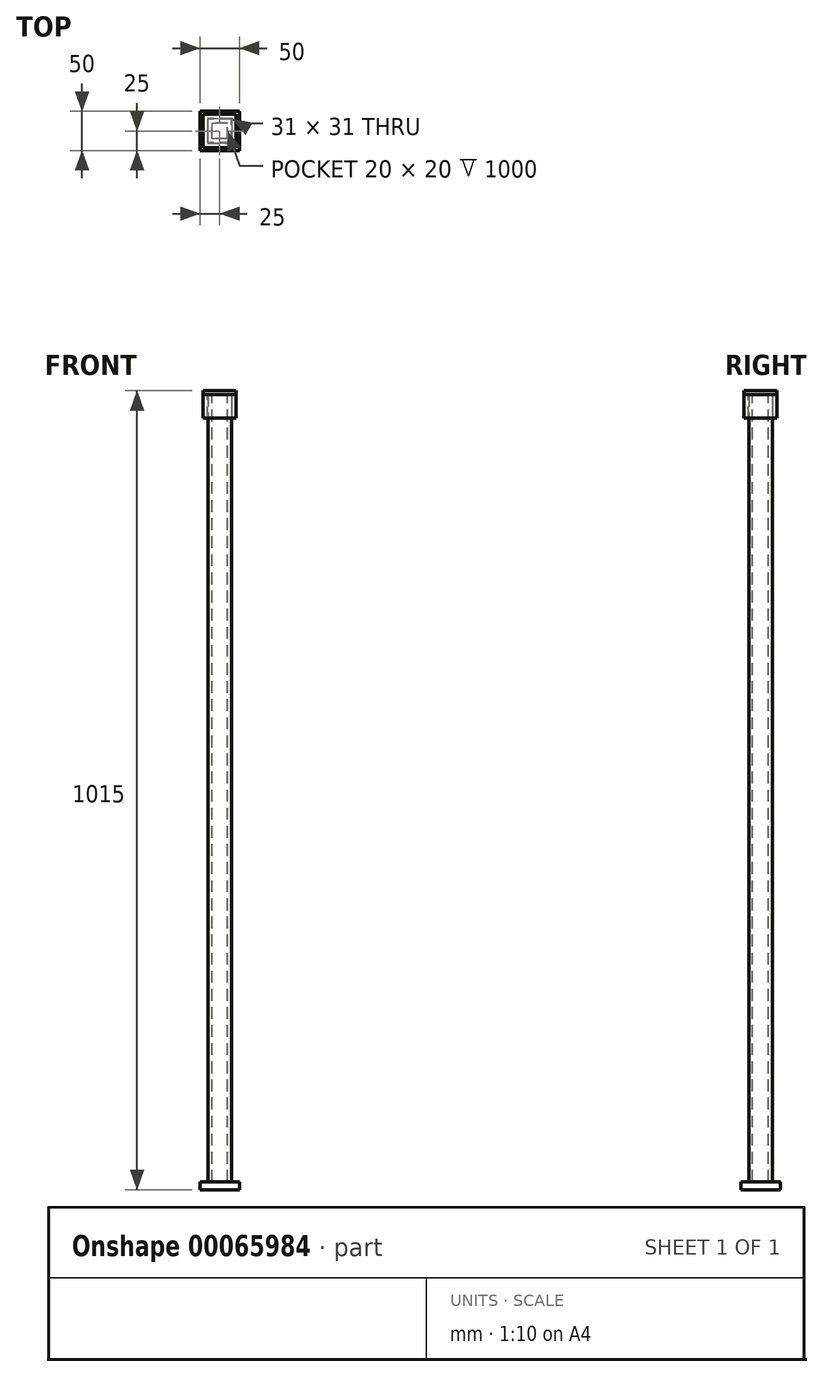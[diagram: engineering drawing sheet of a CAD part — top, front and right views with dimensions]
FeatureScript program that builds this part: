
annotation { "Feature Type Name" : "Feature", "Feature Type Description" : "" }
export const myFeature = defineFeature(function(context is Context, id is Id, definition is map)
    precondition{}
    {
        {
            var Q0;
            Q0=qCreatedBy(makeId("Right.planeOp"),FACE);
            var sketch = newSketch(context, id + "F0", { "sketchPlane" : qUnion([Q0])});
            skLineSegment(sketch, "E0", {"start": v(0, 0) * mm, "end": v(100, 0) * mm, "construction": true});
            skLineSegment(sketch, "E1", {"start": v(100, 0) * mm, "end": v(100, -50) * mm, "construction": true});
            skLineSegment(sketch, "E2", {"start": v(100, -50) * mm, "end": v(200, -50) * mm, "construction": true});
            skLineSegment(sketch, "E3", {"start": v(200, -50) * mm, "end": v(200, -100) * mm, "construction": true});
            skLineSegment(sketch, "E4", {"start": v(200, -100) * mm, "end": v(300, -100) * mm, "construction": true});
            skLineSegment(sketch, "E5", {"start": v(300, -100) * mm, "end": v(300, -150) * mm, "construction": true});
            skLineSegment(sketch, "E6", {"start": v(300, -150) * mm, "end": v(400, -150) * mm, "construction": true});
            skLineSegment(sketch, "E7", {"start": v(400, -150) * mm, "end": v(400, -200) * mm, "construction": true});
            skLineSegment(sketch, "E8.bottom", {"start": v(35, 1010) * mm, "end": v(65, 1010) * mm});
            skLineSegment(sketch, "E8.top", {"start": v(35, 10) * mm, "end": v(65, 10) * mm});
            skLineSegment(sketch, "E8.left", {"start": v(35, 1010) * mm, "end": v(35, 10) * mm});
            skLineSegment(sketch, "E8.right", {"start": v(65, 1010) * mm, "end": v(65, 10) * mm});
            skLineSegment(sketch, "E9.bottom", {"start": v(25, 10) * mm, "end": v(35, 10) * mm});
            skLineSegment(sketch, "E9.top", {"start": v(25, 0) * mm, "end": v(75, 0) * mm});
            skLineSegment(sketch, "E9.left", {"start": v(25, 10) * mm, "end": v(25, 0) * mm});
            skLineSegment(sketch, "E9.right", {"start": v(75, 10) * mm, "end": v(75, 0) * mm});
            skPoint(sketch, "E10", {"position": v(50, 10) * mm});
            skLineSegment(sketch, "E11", {"start": v(65, 10) * mm, "end": v(75, 10) * mm});
            skPoint(sketch, "E12", {"position": v(50, 0) * mm});
            skSolve(sketch);
        }
        {
            var Q0;
            Q0=makeQuery(id+"F0.imprint","IMPRINT",FACE,{"disambiguationData":[TD([[makeQuery(id+"F0.imprint","IMPRINT",EDGE,{"derivedFrom":sQuery(id+"F0.wireOp",EDGE,"E8.bottom")}),-1.0]])]});
            extrude(context, id + "F1", {"entities" : qUnion([Q0]), "depth" : 15 * mm, "hasSecondDirection" : true, "secondDirectionOppositeDirection" : true, "secondDirectionDepth" : 15 * mm});
        }
        {
            var Q0;
            Q0=makeQuery(id+"F0.imprint","IMPRINT",FACE,{"disambiguationData":[TD([[makeQuery(id+"F0.imprint","IMPRINT",EDGE,{"derivedFrom":sQuery(id+"F0.wireOp",EDGE,"E8.top")}),-1.0]])]});
            extrude(context, id + "F2", {"entities" : qUnion([Q0]), "operationType" : NewBodyOperationType.ADD, "depth" : 25 * mm, "hasSecondDirection" : true, "secondDirectionOppositeDirection" : true, "secondDirectionDepth" : 25 * mm});
        }
        {
            var Q0;
            Q0=makeQuery(id+"F1.opExtrude","SWEPT_FACE",FACE,{"disambiguationData":[OSD([sQuery(id+"F0.wireOp",EDGE,"E8.bottom")])]});
            var sketch = newSketch(context, id + "F3", { "sketchPlane" : qUnion([Q0])});
            skLineSegment(sketch, "E13.0", {"start": v(10, 40) * mm, "end": v(10, 60) * mm});
            skLineSegment(sketch, "E13.1", {"start": v(10, 40) * mm, "end": v(-10, 40) * mm});
            skLineSegment(sketch, "E13.2", {"start": v(-10, 40) * mm, "end": v(-10, 60) * mm});
            skLineSegment(sketch, "E13.3", {"start": v(10, 60) * mm, "end": v(-10, 60) * mm});
            skSolve(sketch);
        }
        {
            var Q0;
            Q0 = qSketchRegion(id + "F3", true);
            extrude(context, id + "F4", {"entities" : qUnion([Q0]), "operationType" : NewBodyOperationType.REMOVE, "oppositeDirection" : true, "depth" : 1000 * mm});
        }
        {
            var Q0;
            Q0=makeQuery(id+"F1.opExtrude","SWEPT_FACE",FACE,{"disambiguationData":[OSD([sQuery(id+"F0.wireOp",EDGE,"E8.bottom")])]});
            var sketch = newSketch(context, id + "F5", { "sketchPlane" : qUnion([Q0])});
            skLineSegment(sketch, "E14.0", {"start": v(21, 29) * mm, "end": v(-21, 29) * mm});
            skLineSegment(sketch, "E14.1", {"start": v(21, 29) * mm, "end": v(21, 71) * mm});
            skLineSegment(sketch, "E14.2", {"start": v(21, 71) * mm, "end": v(-21, 71) * mm});
            skLineSegment(sketch, "E14.3", {"start": v(-21, 29) * mm, "end": v(-21, 71) * mm});
            skLineSegment(sketch, "E15.0", {"start": v(-15.5, 65.5) * mm, "end": v(-15.5, 34.5) * mm});
            skLineSegment(sketch, "E15.1", {"start": v(15.5, 65.5) * mm, "end": v(-15.5, 65.5) * mm});
            skLineSegment(sketch, "E15.2", {"start": v(15.5, 34.5) * mm, "end": v(15.5, 65.5) * mm});
            skLineSegment(sketch, "E15.3", {"start": v(-15.5, 34.5) * mm, "end": v(15.5, 34.5) * mm});
            skSolve(sketch);
        }
        {
            var Q0;
            Q0 = qSketchRegion(id + "F5", true);
            extrude(context, id + "F6", {"entities" : qUnion([Q0]), "oppositeDirection" : true, "depth" : 30 * mm});
        }
        {
            var Q0;
            Q0=makeQuery(id+"F6.opExtrude","CAP_FACE",FACE,{"disambiguationData":[OSD([sQuery(id+"F5.wireOp",EDGE,"E14.0"),sQuery(id+"F5.wireOp",EDGE,"E14.1"),sQuery(id+"F5.wireOp",EDGE,"E14.2"),sQuery(id+"F5.wireOp",EDGE,"E14.3"),sQuery(id+"F5.wireOp",EDGE,"E15.0"),sQuery(id+"F5.wireOp",EDGE,"E15.1"),sQuery(id+"F5.wireOp",EDGE,"E15.2"),sQuery(id+"F5.wireOp",EDGE,"E15.3")])],"isStart":true});
            var sketch = newSketch(context, id + "F7", { "sketchPlane" : qUnion([Q0])});
            skLineSegment(sketch, "E16.0", {"start": v(-21, 29) * mm, "end": v(21, 29) * mm});
            skLineSegment(sketch, "E16.1", {"start": v(-21, 71) * mm, "end": v(-21, 29) * mm});
            skLineSegment(sketch, "E16.2", {"start": v(21, 71) * mm, "end": v(-21, 71) * mm});
            skLineSegment(sketch, "E16.3", {"start": v(21, 29) * mm, "end": v(21, 71) * mm});
            skSolve(sketch);
        }
        {
            var Q0;
            Q0 = qSketchRegion(id + "F7", true);
            extrude(context, id + "F8", {"entities" : qUnion([Q0]), "depth" : 5 * mm});
        }
    });
